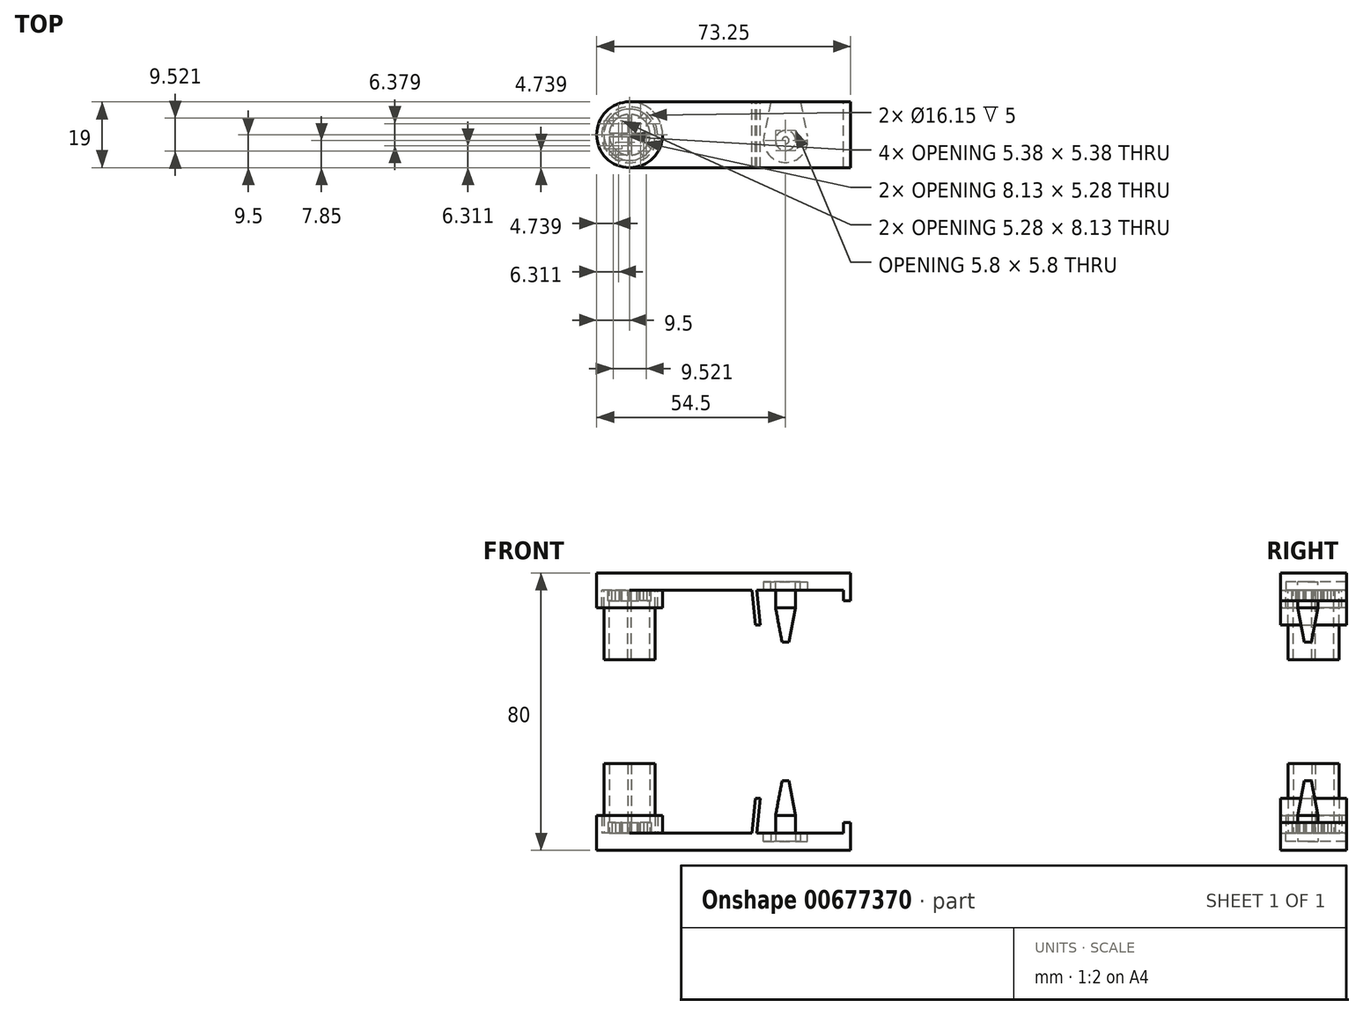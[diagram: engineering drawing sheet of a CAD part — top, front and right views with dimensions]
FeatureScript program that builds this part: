
annotation { "Feature Type Name" : "Feature", "Feature Type Description" : "" }
export const myFeature = defineFeature(function(context is Context, id is Id, definition is map)
    precondition{}
    {
        {
            var Q0;
            Q0=qCreatedBy(makeId("Front.planeOp"),FACE);
            cPlane(context, id + "F0", {"entities" : qUnion([Q0]), "cplaneType" : CPlaneType.OFFSET, "offset" : (9.5 - 2 - 11.7 / 2) * mm, "width" : 150 * mm, "height" : 150 * mm});
        }
        {
            var Q0;
            Q0=qCreatedBy(makeId("Top.planeOp"),FACE);
            var sketch = newSketch(context, id + "F1", { "sketchPlane" : qUnion([Q0])});
            skCircle(sketch, "E0", {"center": v(0, 0) * mm, "radius": 7.4 * mm});
            skArc(sketch, "E1", {"start": v(-5.88, -0.5) * mm, "mid": v(-4.17, -4.17) * mm, "end": v(-0.5, -5.88) * mm});
            skLineSegment(sketch, "E2.left", {"start": v(-0.5, 5.88) * mm, "end": v(-0.5, 0.5) * mm});
            skLineSegment(sketch, "E2.right", {"start": v(0.5, 5.88) * mm, "end": v(0.5, 0.5) * mm});
            skLineSegment(sketch, "E3.bottom", {"start": v(-5.88, 0.5) * mm, "end": v(-0.5, 0.5) * mm});
            skLineSegment(sketch, "E3.top", {"start": v(-5.88, -0.5) * mm, "end": v(-0.5, -0.5) * mm});
            skArc(sketch, "E4.trimOffspring", {"start": v(5.88, 0.5) * mm, "mid": v(4.17, 4.17) * mm, "end": v(0.5, 5.88) * mm});
            skArc(sketch, "E5.trimOffspring", {"start": v(0.5, -5.88) * mm, "mid": v(4.17, -4.17) * mm, "end": v(5.88, -0.5) * mm});
            skArc(sketch, "E6.trimOffspring", {"start": v(-0.5, 5.88) * mm, "mid": v(-4.17, 4.17) * mm, "end": v(-5.88, 0.5) * mm});
            skLineSegment(sketch, "E7.trimOffspring", {"start": v(0.5, 0.5) * mm, "end": v(5.88, 0.5) * mm});
            skLineSegment(sketch, "E8.trimOffspring", {"start": v(0.5, -0.5) * mm, "end": v(0.5, -5.88) * mm});
            skLineSegment(sketch, "E9.trimOffspring", {"start": v(-0.5, -0.5) * mm, "end": v(-0.5, -5.88) * mm});
            skLineSegment(sketch, "E10.trimOffspring", {"start": v(0.5, -0.5) * mm, "end": v(5.88, -0.5) * mm});
            skSolve(sketch);
        }
        {
            var Q0;
            Q0 = qSketchRegion(id + "F1", true);
            extrude(context, id + "F2", {"entities" : qUnion([Q0]), "depth" : 20 * mm, "offsetDistance" : 25 * mm});
        }
        {
            var Q0;
            Q0=qCreatedBy(makeId("Top.planeOp"),FACE);
            var sketch = newSketch(context, id + "F3", { "sketchPlane" : qUnion([Q0])});
            skCircle(sketch, "E11", {"center": v(0, 0) * mm, "radius": 8.07 * mm});
            skCircle(sketch, "E12", {"center": v(0, 0) * mm, "radius": 9.5 * mm});
            skSolve(sketch);
        }
        {
            var Q0;
            Q0 = qSketchRegion(id + "F3", true);
            extrude(context, id + "F4", {"entities" : qUnion([Q0]), "operationType" : NewBodyOperationType.ADD, "depth" : 5 * mm, "offsetDistance" : 25 * mm});
        }
        {
            var Q0;
            Q0=qCreatedBy(makeId("Top.planeOp"),FACE);
            var sketch = newSketch(context, id + "F5", { "sketchPlane" : qUnion([Q0])});
            skLineSegment(sketch, "E13", {"start": v(-4.06, 6.18) * mm, "end": v(0, 2.12) * mm});
            skLineSegment(sketch, "E14", {"start": v(4.06, -6.18) * mm, "end": v(0, -2.12) * mm});
            skArc(sketch, "E15", {"start": v(-6.18, 4.06) * mm, "mid": v(-5.23, 5.23) * mm, "end": v(-4.06, 6.18) * mm});
            skArc(sketch, "E16", {"start": v(4.06, -6.18) * mm, "mid": v(5.23, -5.23) * mm, "end": v(6.18, -4.06) * mm});
            skLineSegment(sketch, "E17", {"start": v(-4.06, -6.18) * mm, "end": v(0, -2.12) * mm});
            skLineSegment(sketch, "E18", {"start": v(4.06, 6.18) * mm, "end": v(0, 2.12) * mm});
            skArc(sketch, "E19", {"start": v(6.18, 4.06) * mm, "mid": v(5.23, 5.23) * mm, "end": v(4.06, 6.18) * mm});
            skArc(sketch, "E20", {"start": v(-4.06, -6.18) * mm, "mid": v(-5.23, -5.23) * mm, "end": v(-6.18, -4.06) * mm});
            skLineSegment(sketch, "E21.trimOffspring", {"start": v(2.12, 0) * mm, "end": v(6.18, 4.06) * mm});
            skLineSegment(sketch, "E22.trimOffspring", {"start": v(2.12, 0) * mm, "end": v(6.18, -4.06) * mm});
            skLineSegment(sketch, "E23.trimOffspring", {"start": v(-2.12, 0) * mm, "end": v(-6.18, -4.06) * mm});
            skLineSegment(sketch, "E24.trimOffspring", {"start": v(-2.12, 0) * mm, "end": v(-6.18, 4.06) * mm});
            skSolve(sketch);
        }
        {
            var Q0;
            Q0 = qSketchRegion(id + "F5", true);
            extrude(context, id + "F6", {"entities" : qUnion([Q0]), "operationType" : NewBodyOperationType.REMOVE, "depth" : 3 * mm, "offsetDistance" : 25 * mm});
        }
        {
            var Q0;
            Q0=qCreatedBy(id+"F0.planeOp",FACE);
            var sketch = newSketch(context, id + "F7", { "sketchPlane" : qUnion([Q0])});
            skLineSegment(sketch, "E25", {"start": v(45, 15) * mm, "end": v(46, 15) * mm});
            skLineSegment(sketch, "E26", {"start": v(46, 15) * mm, "end": v(47.9, 5) * mm});
            skLineSegment(sketch, "E27", {"start": v(47.9, 5) * mm, "end": v(47.9, 0) * mm});
            skLineSegment(sketch, "E28", {"start": v(47.9, 0) * mm, "end": v(45, 0) * mm});
            skLineSegment(sketch, "E29", {"start": v(45, 0) * mm, "end": v(45, 15) * mm});
            skSolve(sketch);
        }
        {
            var Q0;
            Q0 = qSketchRegion(id + "F7", true);
            var Q1;
            Q1=sQuery(id+"F7.wireOp",EDGE,"E29");
            revolve(context, id + "F8", {"operationType" : NewBodyOperationType.ADD, "surfaceOperationType" : NewSurfaceOperationType.NEW, "entities" : qUnion([Q0]), "axis" : qUnion([Q1]), "revolveType" : RevolveType.FULL});
        }
        {
            var Q0;
            Q0=qCreatedBy(makeId("Top.planeOp"),FACE);
            var sketch = newSketch(context, id + "F9", { "sketchPlane" : qUnion([Q0])});
            skArc(sketch, "E30", {"start": v(0, 9.5) * mm, "mid": v(-9.5, 0) * mm, "end": v(0, -9.5) * mm});
            skLineSegment(sketch, "E31", {"start": v(0, 9.5) * mm, "end": v(63.75, 9.5) * mm});
            skLineSegment(sketch, "E32", {"start": v(0, -9.5) * mm, "end": v(63.75, -9.5) * mm});
            skLineSegment(sketch, "E33", {"start": v(63.75, 9.5) * mm, "end": v(63.75, -9.5) * mm});
            skSolve(sketch);
        }
        {
            var Q0;
            Q0 = qSketchRegion(id + "F9", true);
            extrude(context, id + "F10", {"entities" : qUnion([Q0]), "operationType" : NewBodyOperationType.ADD, "oppositeDirection" : true, "depth" : 5 * mm, "offsetDistance" : 25 * mm});
        }
        {
            var Q0;
            Q0=qCreatedBy(makeId("Front.planeOp"),FACE);
            var sketch = newSketch(context, id + "F11", { "sketchPlane" : qUnion([Q0])});
            skLineSegment(sketch, "E34.bottom", {"start": v(63.75, 0) * mm, "end": v(61.75, 0) * mm});
            skLineSegment(sketch, "E34.top", {"start": v(63.75, 3) * mm, "end": v(61.75, 3) * mm});
            skLineSegment(sketch, "E34.left", {"start": v(63.75, 0) * mm, "end": v(63.75, 3) * mm});
            skLineSegment(sketch, "E34.right", {"start": v(61.75, 0) * mm, "end": v(61.75, 3) * mm});
            skLineSegment(sketch, "E35.bottom", {"start": v(36.75, 0) * mm, "end": v(35.25, 0) * mm});
            skLineSegment(sketch, "E35.top", {"start": v(37.75, 10) * mm, "end": v(36.25, 10) * mm});
            skLineSegment(sketch, "E35.left", {"start": v(36.75, 0) * mm, "end": v(37.75, 10) * mm});
            skLineSegment(sketch, "E35.right", {"start": v(35.25, 0) * mm, "end": v(36.25, 10) * mm});
            skSolve(sketch);
        }
        {
            var Q0;
            Q0 = qSketchRegion(id + "F11", true);
            extrude(context, id + "F12", {"entities" : qUnion([Q0]), "operationType" : NewBodyOperationType.ADD, "endBound" : BoundingType.SYMMETRIC, "depth" : 19 * mm, "offsetDistance" : 25 * mm});
        }
        {
            var Q0;
            Q0=qCreatedBy(makeId("Top.planeOp"),FACE);
            var sketch = newSketch(context, id + "F13", { "sketchPlane" : qUnion([Q0])});
            skArc(sketch, "E36", {"start": v(39.26, -0.54) * mm, "mid": v(45, -7.5) * mm, "end": v(50.74, -0.54) * mm, "construction": true});
            skArc(sketch, "E37", {"start": v(48.44, 11.37) * mm, "mid": v(45, 14.2) * mm, "end": v(41.56, 11.37) * mm, "construction": true});
            skLineSegment(sketch, "E38", {"start": v(48.44, 11.37) * mm, "end": v(50.74, -0.54) * mm, "construction": true});
            skLineSegment(sketch, "E39", {"start": v(41.56, 11.37) * mm, "end": v(39.26, -0.54) * mm, "construction": true});
            skLineSegment(sketch, "E40", {"start": v(45, 10.7) * mm, "end": v(45, -1.65) * mm, "construction": true});
            skArc(sketch, "E41.0", {"start": v(48.93, 11.46) * mm, "mid": v(45, 14.7) * mm, "end": v(41.07, 11.46) * mm});
            skLineSegment(sketch, "E41.1", {"start": v(48.93, 11.46) * mm, "end": v(51.23, -0.44) * mm});
            skArc(sketch, "E41.2", {"start": v(38.77, -0.44) * mm, "mid": v(45, -8) * mm, "end": v(51.23, -0.44) * mm});
            skLineSegment(sketch, "E41.3", {"start": v(41.07, 11.46) * mm, "end": v(38.77, -0.44) * mm});
            skCircle(sketch, "E42", {"center": v(45, -1.65) * mm, "radius": 2.9 * mm});
            skSolve(sketch);
        }
        {
            var Q0;
            Q0 = qSketchRegion(id + "F13", true);
            extrude(context, id + "F14", {"entities" : qUnion([Q0]), "operationType" : NewBodyOperationType.REMOVE, "oppositeDirection" : true, "depth" : 2.5 * mm, "offsetDistance" : 25 * mm});
        }
        {
            var Q0;
            Q0=qCreatedBy(makeId("Top.planeOp"),FACE);
            cPlane(context, id + "F15", {"entities" : qUnion([Q0]), "cplaneType" : CPlaneType.OFFSET, "offset" : 35 * mm, "width" : 150 * mm, "height" : 150 * mm});
        }
        {
            var Q0;
            Q0=makeQuery(id+"F2.opExtrude","SWEPT_BODY",BODY,{"disambiguationData":[OSD([sQuery(id+"F1.wireOp",EDGE,"E0"),sQuery(id+"F1.wireOp",EDGE,"E1"),sQuery(id+"F1.wireOp",EDGE,"E2.left"),sQuery(id+"F1.wireOp",EDGE,"E2.right"),sQuery(id+"F1.wireOp",EDGE,"E3.bottom"),sQuery(id+"F1.wireOp",EDGE,"E3.top"),sQuery(id+"F1.wireOp",EDGE,"E4.trimOffspring"),sQuery(id+"F1.wireOp",EDGE,"E5.trimOffspring"),sQuery(id+"F1.wireOp",EDGE,"E6.trimOffspring"),sQuery(id+"F1.wireOp",EDGE,"E7.trimOffspring"),sQuery(id+"F1.wireOp",EDGE,"E8.trimOffspring"),sQuery(id+"F1.wireOp",EDGE,"E9.trimOffspring"),sQuery(id+"F1.wireOp",EDGE,"E10.trimOffspring")])]});
            var Q1;
            Q1=qCreatedBy(id+"F15.planeOp",FACE);
            mirror(context, id + "F16", {"entities" : qUnion([Q0]), "mirrorPlane" : qUnion([Q1])});
        }
    });
